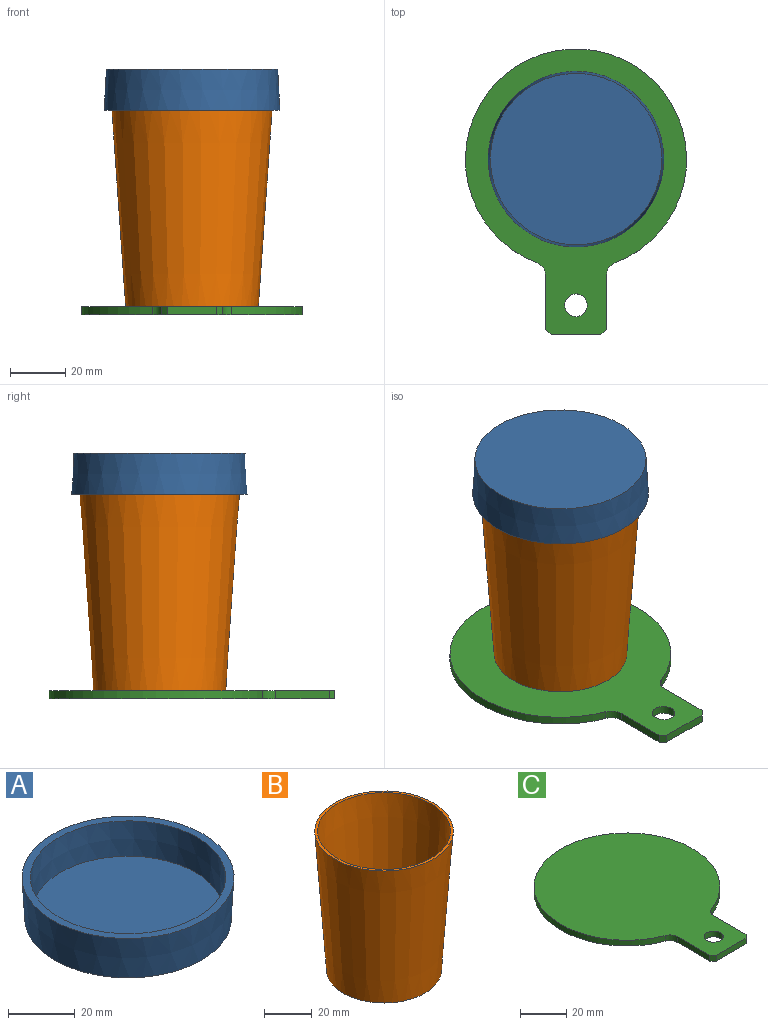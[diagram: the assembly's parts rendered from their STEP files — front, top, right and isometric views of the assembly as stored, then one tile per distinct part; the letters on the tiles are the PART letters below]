
ASSEMBLY  parts=3 mates=2
PART A: 5 faces, bbox 63.6x63.6x15 mm
  f0: cone r=31mm half-angle=3deg, axis (0,0,1), area 2962.8mm2, adj f1,f2
  f1: plane 63.57x63.57mm, normal (0,0,1), area 480.3mm2, adj f0,f3
  f2: plane 62x62mm, normal (0,0,-1), area 3019.1mm2, adj f0
  f3: cone r=28.5mm half-angle=3deg, axis (0,0,1), area 2277.3mm2, adj f1,f4
  f4: plane 57.26x57.26mm, normal (0,0,1), area 2574.7mm2, adj f3
PART B: 5 faces, bbox 57.9x57.9x71 mm
  f0: cone r=24mm half-angle=4deg, axis (0,0,1), area 11842.8mm2, adj f1,f2
  f1: plane 57.93x57.93mm, normal (0,0,1), area 214.4mm2, adj f0,f3
  f2: plane 48x48mm, normal (0,0,-1), area 1809.6mm2, adj f0
  f3: cone r=22.8mm half-angle=4deg, axis (0,0,1), area 11132.2mm2, adj f1,f4
  f4: plane 45.76x45.76mm, normal (0,0,1), area 1644.7mm2, adj f3
PART C: 11 faces, bbox 80x103.5x3 mm
  f0: cylinder r=5mm len=4.67mm, axis (0,0,-1), area 18.1mm2, adj f1,f6,f7,f8
  f1: cylinder r=40mm len=80mm, axis (0,0,-1), area 666.7mm2, adj f0,f2,f7,f8
  f2: cylinder r=5mm len=4.67mm, axis (0,0,-1), area 18.1mm2, adj f1,f3,f7,f8
  f3: plane 19.4x3mm, normal (-1,0,0), area 58.2mm2, adj f2,f7,f8,f9
  f4: plane 18x3mm, normal (0,-1,0), area 54mm2, adj f7,f8,f9,f10
  f5: cylinder r=4.1mm len=8.2mm, axis (0,0,-1), area 77.3mm2, adj f7,f8
  f6: plane 19.4x3mm, normal (1,0,0), area 58.2mm2, adj f0,f7,f8,f10
  f7: plane 103.46x80mm, normal (0,0,1), area 5501.7mm2, adj f0,f1,f2,f3,f4,f5,f6,f9
  f8: plane 103.46x80mm, normal (0,0,-1), area 5501.7mm2, adj f0,f1,f2,f3,f4,f5,f6,f9
  f9: plane 3x2mm, normal (-0.71,-0.71,0), area 8.5mm2, adj f3,f4,f7,f8
  f10: plane 3x2mm, normal (0.71,-0.71,0), area 8.5mm2, adj f4,f6,f7,f8
PLACE A rot(axis=(1,0,0),180deg) t=(0,0,86)mm
PLACE B at identity
PLACE C t=(0,-38.46,-3)mm
MATE cylindrical A.f0 <-> B.f0  axis (0,0,-1) through (0,0,71)mm
MATE cylindrical B.f0 <-> C.f1  axis (0,0,-1) through (0,0,0)mm
